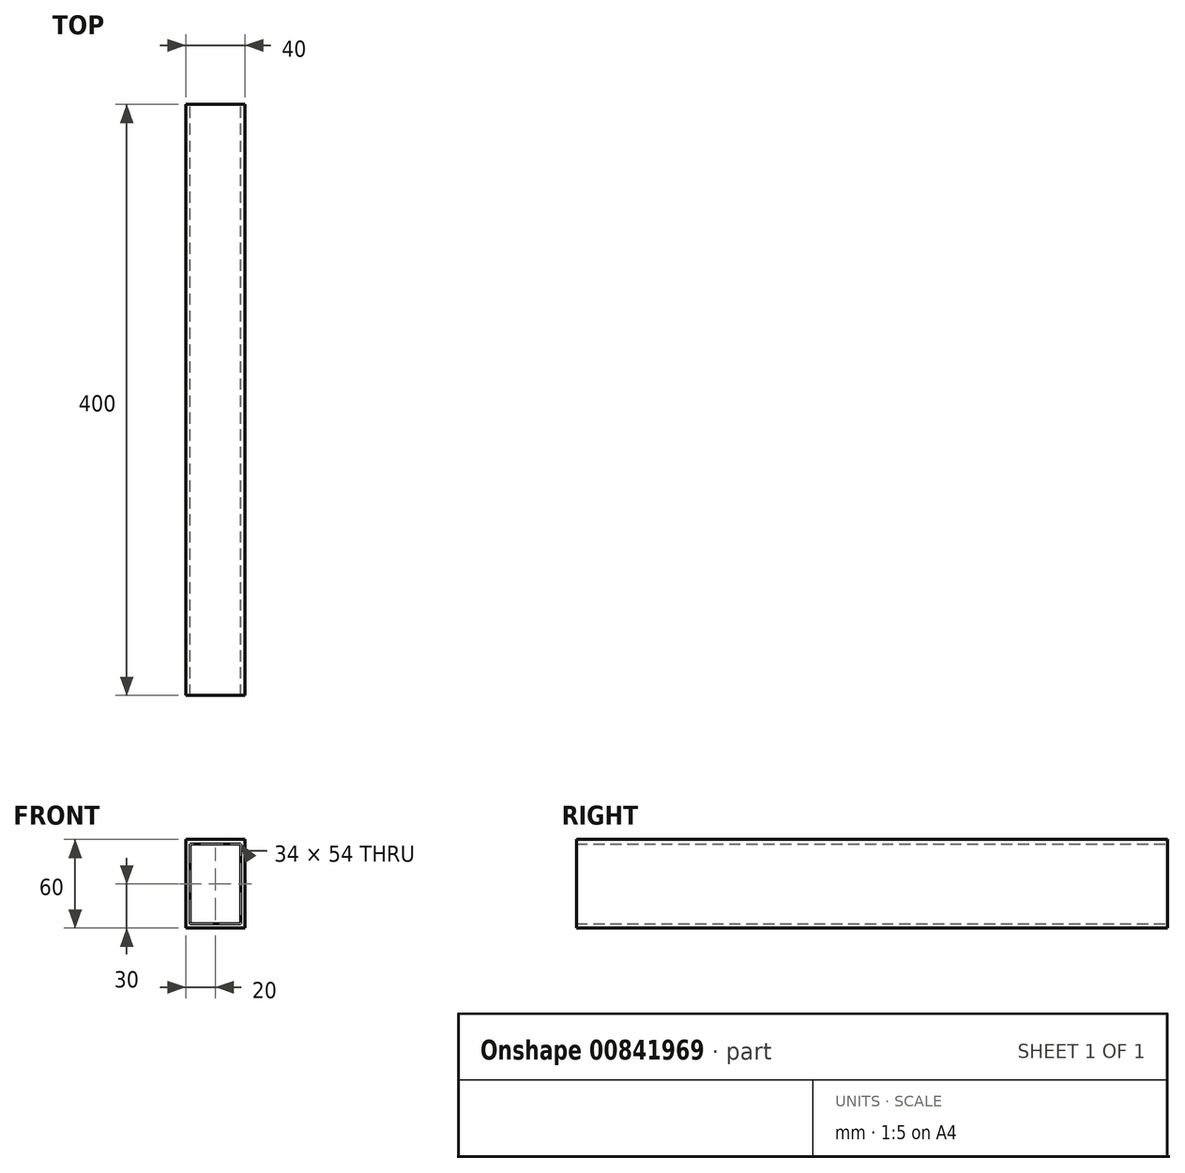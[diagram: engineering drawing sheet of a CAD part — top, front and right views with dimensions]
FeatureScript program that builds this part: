
annotation { "Feature Type Name" : "Feature", "Feature Type Description" : "" }
export const myFeature = defineFeature(function(context is Context, id is Id, definition is map)
    precondition{}
    {
        {
            var Q0;
            Q0=qCreatedBy(makeId("Front.planeOp"),FACE);
            var sketch = newSketch(context, id + "F0", { "sketchPlane" : qUnion([Q0])});
            skLineSegment(sketch, "E0.bottom", {"start": v(-20, 30) * mm, "end": v(20, 30) * mm});
            skLineSegment(sketch, "E0.top", {"start": v(-20, -30) * mm, "end": v(20, -30) * mm});
            skLineSegment(sketch, "E0.left", {"start": v(-20, 30) * mm, "end": v(-20, -30) * mm});
            skLineSegment(sketch, "E0.right", {"start": v(20, 30) * mm, "end": v(20, -30) * mm});
            skLineSegment(sketch, "E1.0", {"start": v(-17, 27) * mm, "end": v(-17, -27) * mm});
            skLineSegment(sketch, "E1.1", {"start": v(-17, 27) * mm, "end": v(17, 27) * mm});
            skLineSegment(sketch, "E1.2", {"start": v(17, 27) * mm, "end": v(17, -27) * mm});
            skLineSegment(sketch, "E1.3", {"start": v(-17, -27) * mm, "end": v(17, -27) * mm});
            skSolve(sketch);
        }
        {
            var Q0;
            Q0=makeQuery(id+"F0.imprint","IMPRINT",FACE,{"disambiguationData":[TD([[makeQuery(id+"F0.imprint","IMPRINT",EDGE,{"derivedFrom":sQuery(id+"F0.wireOp",EDGE,"E0.bottom")}),-1.0]])]});
            extrude(context, id + "F1", {"entities" : qUnion([Q0]), "endBound" : BoundingType.SYMMETRIC, "depth" : 400 * mm, "offsetDistance" : 25 * mm});
        }
    });
